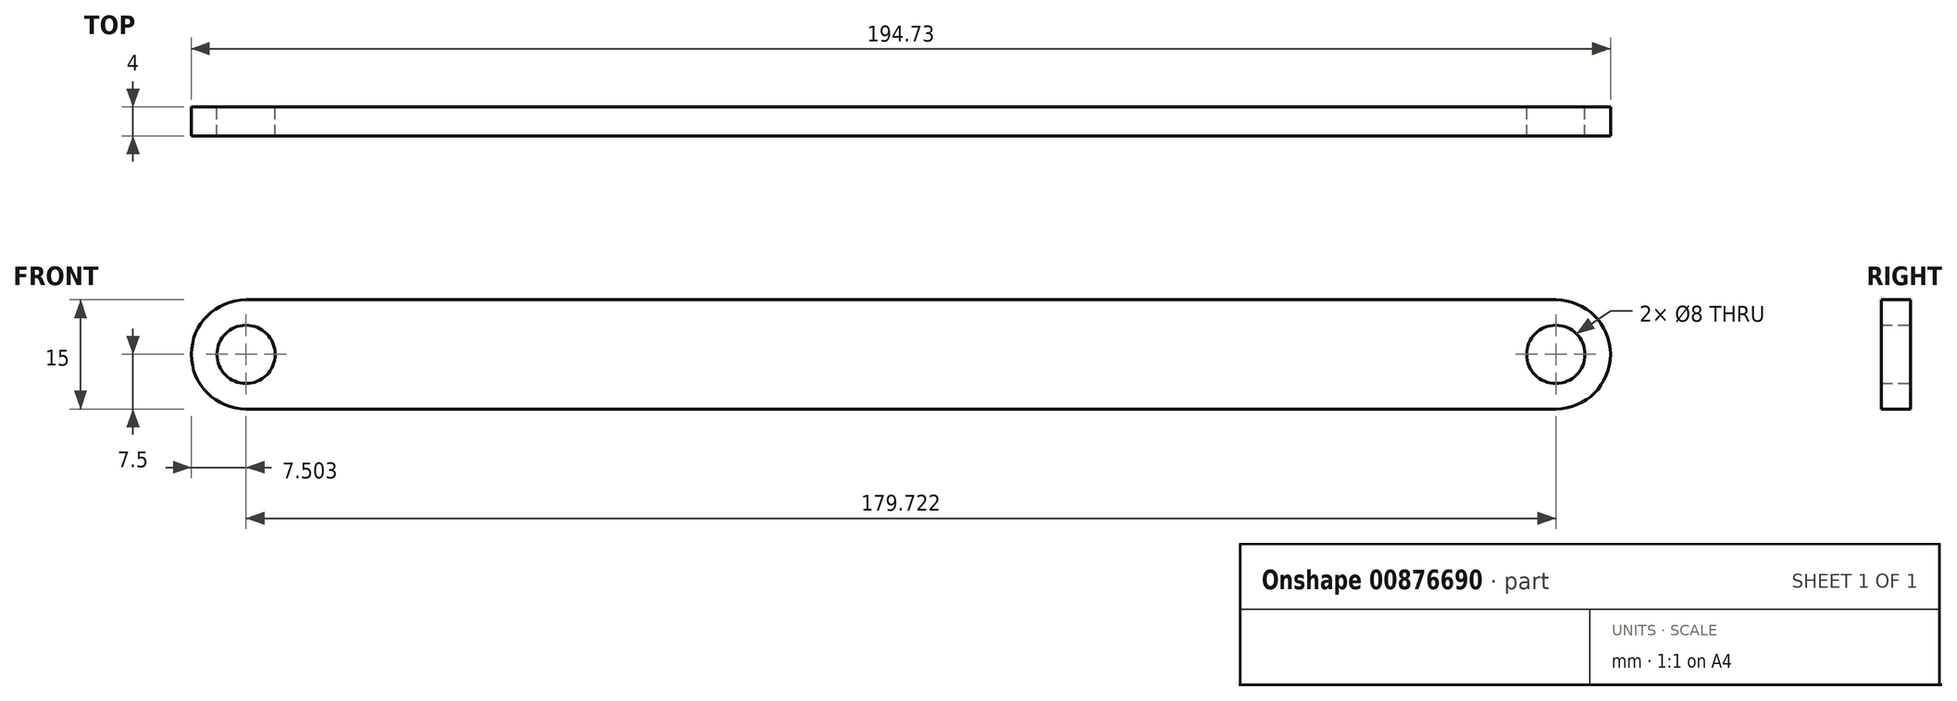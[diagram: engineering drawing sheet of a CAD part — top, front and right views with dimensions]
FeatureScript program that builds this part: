
annotation { "Feature Type Name" : "Feature", "Feature Type Description" : "" }
export const myFeature = defineFeature(function(context is Context, id is Id, definition is map)
    precondition{}
    {
        {
            var Q0;
            Q0=qCreatedBy(makeId("Front.planeOp"),FACE);
            var sketch = newSketch(context, id + "F0", { "sketchPlane" : qUnion([Q0])});
            skCircle(sketch, "E0", {"center": v(85.48, 0) * mm, "radius": 4 * mm});
            skCircle(sketch, "E1", {"center": v(-94.25, 0) * mm, "radius": 4 * mm});
            skArc(sketch, "E2", {"start": v(-94.25, 7.5) * mm, "mid": v(-101.75, 0) * mm, "end": v(-94.25, -7.5) * mm});
            skArc(sketch, "E3", {"start": v(85.48, -7.5) * mm, "mid": v(92.98, 0) * mm, "end": v(85.48, 7.5) * mm});
            skLineSegment(sketch, "E4", {"start": v(-94.25, 7.5) * mm, "end": v(85.48, 7.5) * mm});
            skLineSegment(sketch, "E5", {"start": v(-94.25, -7.5) * mm, "end": v(85.48, -7.5) * mm});
            skSolve(sketch);
        }
        {
            var Q0;
            Q0=makeQuery(id+"F0.imprint","IMPRINT",FACE,{"disambiguationData":[TD([[makeQuery(id+"F0.imprint","IMPRINT",EDGE,{"derivedFrom":sQuery(id+"F0.wireOp",EDGE,"E0")}),-1.0]])]});
            extrude(context, id + "F1", {"entities" : qUnion([Q0]), "depth" : 4 * mm, "offsetDistance" : 25 * mm});
        }
    });
